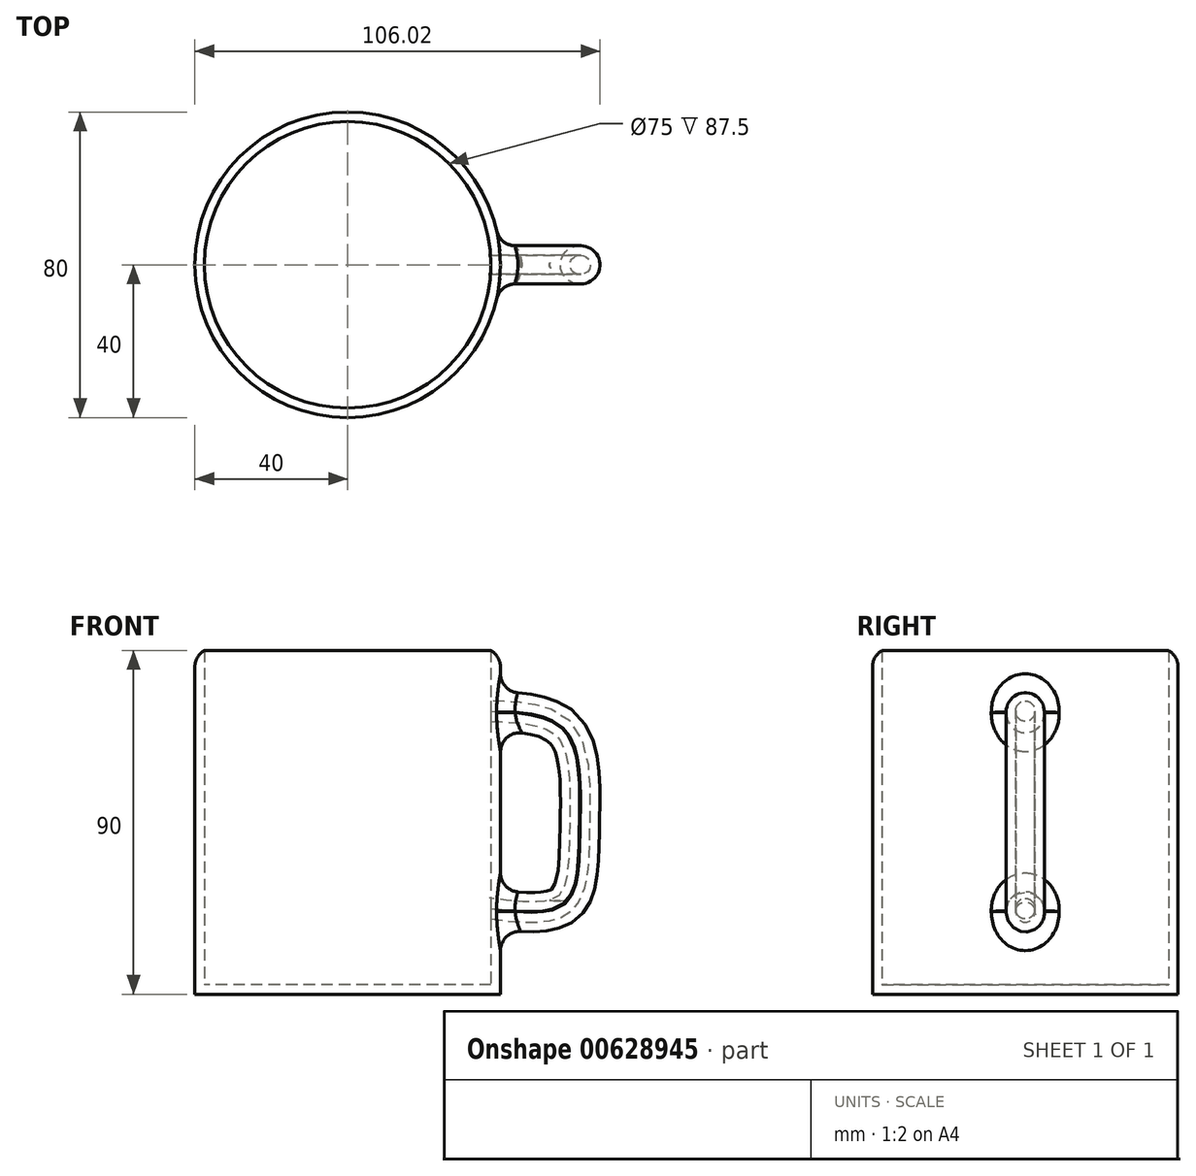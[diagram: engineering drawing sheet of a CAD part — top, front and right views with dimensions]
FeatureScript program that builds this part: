
annotation { "Feature Type Name" : "Feature", "Feature Type Description" : "" }
export const myFeature = defineFeature(function(context is Context, id is Id, definition is map)
    precondition{}
    {
        {
            var Q0;
            Q0=qCreatedBy(makeId("Top.planeOp"),FACE);
            var sketch = newSketch(context, id + "F0", { "sketchPlane" : qUnion([Q0])});
            skCircle(sketch, "E0", {"center": v(0, 0) * mm, "radius": 40 * mm});
            skSolve(sketch);
        }
        {
            var Q0;
            Q0 = qSketchRegion(id + "F0", true);
            extrude(context, id + "F1", {"entities" : qUnion([Q0]), "depth" : 95 * mm, "offsetDistance" : 25 * mm});
        }
        {
            var Q0;
            Q0=qCreatedBy(makeId("Front.planeOp"),FACE);
            var sketch = newSketch(context, id + "F2", { "sketchPlane" : qUnion([Q0])});
            skFitSpline(sketch, "E1", {"points": [v(35.08, 74.87) * mm, v(57.4, 69.5) * mm, v(61.43, 43.68) * mm, v(57.13, 23.25) * mm, v(34.28, 22.18) * mm], "startDerivative": vector(107.98, -2.54) * mm, "endDerivative": vector(-111.14, 15.84) * mm});
            skSolve(sketch);
        }
        {
            var Q0;
            Q0=qCreatedBy(makeId("Right.planeOp"),FACE);
            cPlane(context, id + "F3", {"entities" : qUnion([Q0]), "cplaneType" : CPlaneType.OFFSET, "offset" : 34.1 * mm, "width" : 150 * mm, "height" : 150 * mm});
        }
        {
            var Q0;
            Q0=qCreatedBy(id+"F3.planeOp",FACE);
            var sketch = newSketch(context, id + "F4", { "sketchPlane" : qUnion([Q0])});
            skCircle(sketch, "E2", {"center": v(0, 74.38) * mm, "radius": 5 * mm});
            skSolve(sketch);
        }
        {
            var Q0;
            Q0=qCreatedBy(id+"F3.planeOp",FACE);
            var sketch = newSketch(context, id + "F5", { "sketchPlane" : qUnion([Q0])});
            skCircle(sketch, "E3", {"center": v(0, 23.1) * mm, "radius": 5 * mm});
            skSolve(sketch);
        }
        {
            var Q0;
            Q0 = qSketchRegion(id + "F4", true);
            var Q1;
            Q1 = qSketchRegion(id + "F5", true);
            var Q2;
            Q2 = qConstructionFilter(qBodyType(qCreatedBy(id + "F2" ,EDGE), BodyType.WIRE), ConstructionObject.NO);
            sweep(context, id + "F6", {"operationType" : NewBodyOperationType.ADD, "profiles" : qUnion([Q0, Q1]), "path" : qUnion([Q2])});
        }
        {
            var Q0;
            Q0=makeQuery(id+"F1.opExtrude","CAP_FACE",FACE,{"disambiguationData":[OSD([sQuery(id+"F0.wireOp",EDGE,"E0")])],"isStart":false});
            shell(context, id + "F7", {"entities" : qUnion([Q0]), "thickness" : 2.5 * mm});
        }
        {
            var Q0;
            Q0=makeQuery(id+"F6.opSweep","SWEPT_FACE",FACE,{"disambiguationData":[OSD([sQuery(id+"F2.wireOp",EDGE,"E1"),sQuery(id+"F4.wireOp",EDGE,"E2")])]});
            var Q1;
            Q1=makeQuery(id+"F6.opSweep","SWEPT_FACE",FACE,{"disambiguationData":[OSD([sQuery(id+"F2.wireOp",EDGE,"E1"),sQuery(id+"F5.wireOp",EDGE,"E3")])]});
            fillet(context, id + "F8", {"entities" : qUnion([Q0, Q1]), "radius" : 5 * mm, "tangentPropagation" : true, "allowEdgeOverflow" : false});
        }
        {
            var Q0;
            {var subQ0=sQuery(id+"F0.wireOp",EDGE,"E0");Q0=makeQuery(id+"F7.opShell","OFFSET_EDGE",EDGE,{"disambiguationData":[OSD([subQ0]),TDD([makeQuery(id+"F1.opExtrude","CAP_EDGE",EDGE,{"disambiguationData":[OSD([subQ0])],"isStart":false})])]});}
            chamfer(context, id + "F9", {"entities" : qUnion([Q0]), "width" : 5 * mm, "tangentPropagation" : true});
        }
        {
            var Q0;
            {var subQ0=sQuery(id+"F0.wireOp",EDGE,"E0");Q0=makeQuery(id+"F9.opChamfer","BLEND_EDGE",EDGE,{"blendedFrom":[makeQuery(id+"F7.opShell","OFFSET_EDGE",EDGE,{"disambiguationData":[OSD([subQ0]),TDD([makeQuery(id+"F1.opExtrude","CAP_EDGE",EDGE,{"disambiguationData":[OSD([subQ0])],"isStart":false})])]}),makeQuery(id+"F1.opExtrude","SWEPT_FACE",FACE,{"disambiguationData":[OSD([subQ0])]})],"blendedInto":[makeQuery(id+"F1.opExtrude","SWEPT_FACE",FACE,{"disambiguationData":[OSD([subQ0])]})]});}
            fillet(context, id + "F10", {"entities" : qUnion([Q0]), "radius" : 5 * mm, "tangentPropagation" : true, "allowEdgeOverflow" : false});
        }
    });
